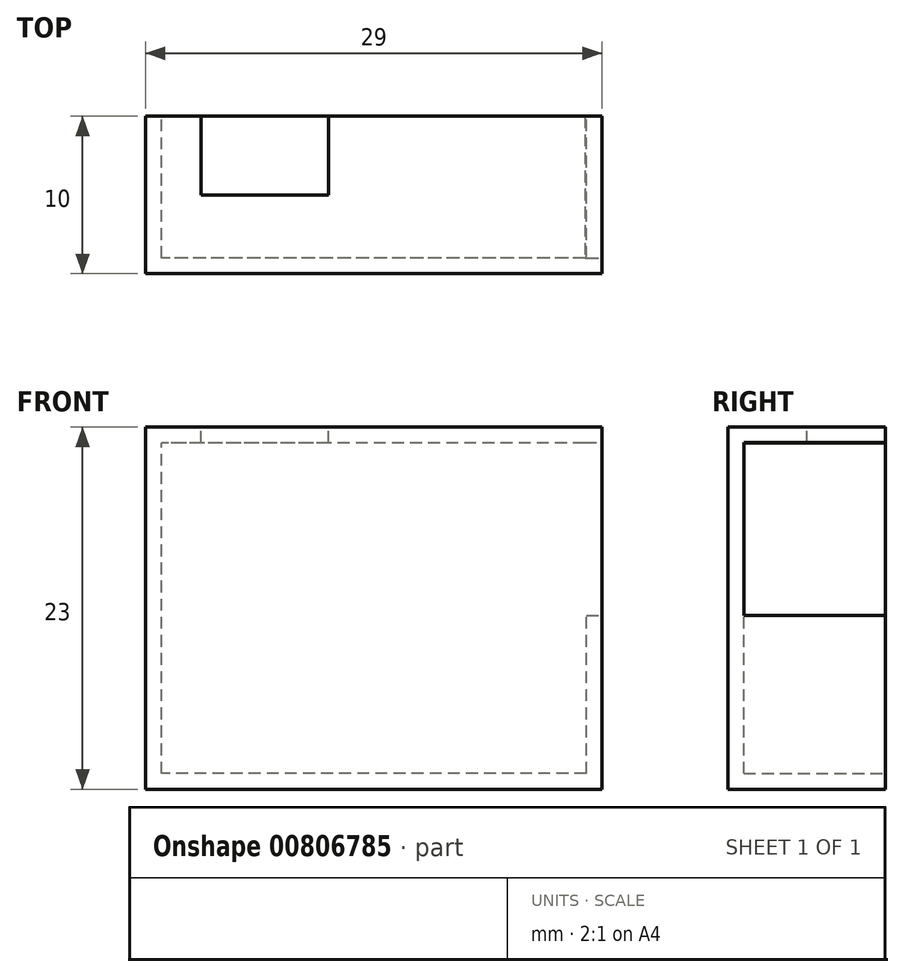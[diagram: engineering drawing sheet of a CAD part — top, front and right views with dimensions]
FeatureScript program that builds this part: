
annotation { "Feature Type Name" : "Feature", "Feature Type Description" : "" }
export const myFeature = defineFeature(function(context is Context, id is Id, definition is map)
    precondition{}
    {
        {
            var Q0;
            Q0=qCreatedBy(makeId("Front.planeOp"),FACE);
            var sketch = newSketch(context, id + "F0", { "sketchPlane" : qUnion([Q0])});
            skLineSegment(sketch, "E0.bottom", {"start": v(13.5, -10.5) * mm, "end": v(-13.5, -10.5) * mm});
            skLineSegment(sketch, "E0.top", {"start": v(13.5, 10.5) * mm, "end": v(-13.5, 10.5) * mm});
            skLineSegment(sketch, "E0.left", {"start": v(13.5, -10.5) * mm, "end": v(13.5, 10.5) * mm});
            skLineSegment(sketch, "E0.right", {"start": v(-13.5, -10.5) * mm, "end": v(-13.5, 10.5) * mm});
            skPoint(sketch, "E0.middle", {"position": v(0, 0) * mm});
            skLineSegment(sketch, "E1.bottom", {"start": v(14.5, -11.5) * mm, "end": v(-14.5, -11.5) * mm});
            skLineSegment(sketch, "E1.top", {"start": v(14.5, 11.5) * mm, "end": v(-14.5, 11.5) * mm});
            skLineSegment(sketch, "E1.left", {"start": v(14.5, -11.5) * mm, "end": v(14.5, 11.5) * mm});
            skLineSegment(sketch, "E1.right", {"start": v(-14.5, -11.5) * mm, "end": v(-14.5, 11.5) * mm});
            skSolve(sketch);
        }
        {
            var Q0;
            Q0=makeQuery(id+"F0.imprint","IMPRINT",FACE,{"disambiguationData":[TD([[makeQuery(id+"F0.imprint","IMPRINT",EDGE,{"derivedFrom":sQuery(id+"F0.wireOp",EDGE,"E0.bottom")}),1.0]])]});
            var Q1;
            Q1=makeQuery(id+"F0.imprint","IMPRINT",FACE,{"disambiguationData":[TD([[makeQuery(id+"F0.imprint","IMPRINT",EDGE,{"derivedFrom":sQuery(id+"F0.wireOp",EDGE,"E0.bottom")}),-1.0]])]});
            extrude(context, id + "F1", {"entities" : qUnion([Q0, Q1]), "depth" : 10 * mm, "offsetDistance" : 25 * mm});
        }
        {
            var Q0;
            Q0=makeQuery(id+"F0.imprint","IMPRINT",FACE,{"disambiguationData":[TD([[makeQuery(id+"F0.imprint","IMPRINT",EDGE,{"derivedFrom":sQuery(id+"F0.wireOp",EDGE,"E0.bottom")}),-1.0]])]});
            extrude(context, id + "F2", {"entities" : qUnion([Q0]), "operationType" : NewBodyOperationType.REMOVE, "depth" : 9 * mm, "offsetDistance" : 25 * mm});
        }
        {
            var Q0;
            Q0=makeQuery(id+"F0.imprint","IMPRINT",FACE,{"disambiguationData":[TD([[makeQuery(id+"F0.imprint","IMPRINT",EDGE,{"derivedFrom":sQuery(id+"F0.wireOp",EDGE,"E0.bottom")}),1.0]])]});
            var sketch = newSketch(context, id + "F3", { "sketchPlane" : qUnion([Q0])});
            skLineSegment(sketch, "E2", {"start": v(13.4, 10.53) * mm, "end": v(13.4, -0.47) * mm});
            skLineSegment(sketch, "E3", {"start": v(13.4, -0.47) * mm, "end": v(14.64, -0.47) * mm});
            skLineSegment(sketch, "E4", {"start": v(14.64, -0.47) * mm, "end": v(14.64, 10.53) * mm});
            skLineSegment(sketch, "E5", {"start": v(13.4, 10.53) * mm, "end": v(15.75, 10.53) * mm});
            skSolve(sketch);
        }
        {
            var Q0;
            Q0 = qSketchRegion(id + "F3", true);
            extrude(context, id + "F4", {"entities" : qUnion([Q0]), "operationType" : NewBodyOperationType.REMOVE, "depth" : 9 * mm, "offsetDistance" : 25 * mm});
        }
        {
            var Q0;
            Q0=makeQuery(id+"F0.imprint","IMPRINT",FACE,{"disambiguationData":[TD([[makeQuery(id+"F0.imprint","IMPRINT",EDGE,{"derivedFrom":sQuery(id+"F0.wireOp",EDGE,"E0.bottom")}),1.0]])]});
            var sketch = newSketch(context, id + "F5", { "sketchPlane" : qUnion([Q0])});
            skLineSegment(sketch, "E6.bottom", {"start": v(-13.52, 10.52) * mm, "end": v(-10.97, 10.52) * mm});
            skLineSegment(sketch, "E6.top", {"start": v(-13.52, 11.56) * mm, "end": v(-10.97, 11.56) * mm});
            skLineSegment(sketch, "E6.left", {"start": v(-13.52, 10.52) * mm, "end": v(-13.52, 11.56) * mm});
            skLineSegment(sketch, "E6.right", {"start": v(-10.97, 10.52) * mm, "end": v(-10.97, 11.56) * mm});
            skLineSegment(sketch, "E7.bottom", {"start": v(-10.97, 10.13) * mm, "end": v(-2.89, 10.13) * mm});
            skLineSegment(sketch, "E7.top", {"start": v(-10.97, 11.86) * mm, "end": v(-2.89, 11.86) * mm});
            skLineSegment(sketch, "E7.left", {"start": v(-10.97, 10.13) * mm, "end": v(-10.97, 11.86) * mm});
            skLineSegment(sketch, "E7.right", {"start": v(-2.89, 10.13) * mm, "end": v(-2.89, 11.86) * mm});
            skSolve(sketch);
        }
        {
            var Q0;
            {var subQ1=sQuery(id+"F5.wireOp",EDGE,"E7.top");Q0=makeQuery(id+"F5.imprint","IMPRINT",FACE,{"disambiguationData":[TD([[makeQuery(id+"F5.imprint","IMPRINT",EDGE,{"derivedFrom":subQ1}),-1.0]])]});}
            var Q1;
            {var subQ0=sQuery(id+"F5.wireOp",EDGE,"E7.bottom");Q1=makeQuery(id+"F5.imprint","IMPRINT",FACE,{"disambiguationData":[TD([[makeQuery(id+"F5.imprint","IMPRINT",EDGE,{"derivedFrom":subQ0}),1.0]])]});}
            var Q2;
            {var subQ0=sQuery(id+"F5.wireOp",EDGE,"E7.left");var subQ1=makeQuery(id+"F5.imprint","INTERSECT",VERTEX,{"derivedFrom":[sQuery(id+"F5.wireOp",EDGE,"E6.bottom"),subQ0]});Q2=makeQuery(id+"F5.imprint","IMPRINT",FACE,{"disambiguationData":[TD([[makeQuery(id+"F5.imprint","IMPRINT",EDGE,{"disambiguationData":[TD([[subQ1,1.0]])],"derivedFrom":subQ0}),-1.0]])]});}
            extrude(context, id + "F6", {"entities" : qUnion([Q0, Q1, Q2]), "operationType" : NewBodyOperationType.REMOVE, "depth" : 5 * mm, "offsetDistance" : 25 * mm});
        }
    });
